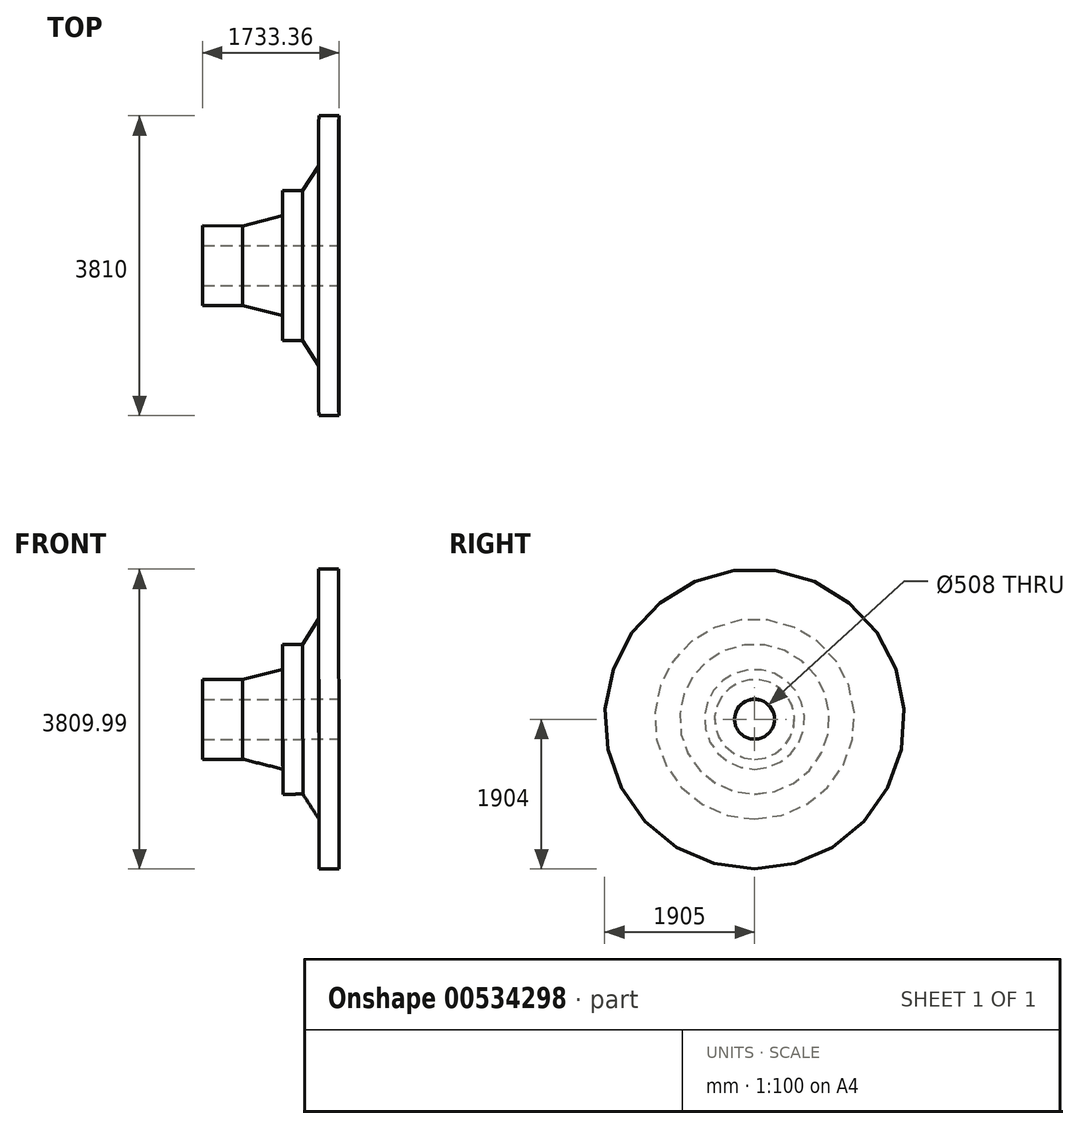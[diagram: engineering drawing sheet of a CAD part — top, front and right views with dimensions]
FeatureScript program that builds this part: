
annotation { "Feature Type Name" : "Feature", "Feature Type Description" : "" }
export const myFeature = defineFeature(function(context is Context, id is Id, definition is map)
    precondition{}
    {
        {
            var Q0;
            Q0=qCreatedBy(makeId("Front.planeOp"),FACE);
            var sketch = newSketch(context, id + "F0", { "sketchPlane" : qUnion([Q0])});
            skLineSegment(sketch, "E0", {"start": v(-1122.68, -2.8) * mm, "end": v(-1122.68, 251.2) * mm});
            skLineSegment(sketch, "E1", {"start": v(-1122.68, 251.2) * mm, "end": v(-614.68, 251.2) * mm});
            skLineSegment(sketch, "E2", {"start": v(-614.68, 251.2) * mm, "end": v(-106.68, 379.85) * mm});
            skLineSegment(sketch, "E3", {"start": v(-106.68, 379.85) * mm, "end": v(-106.68, 697.35) * mm});
            skLineSegment(sketch, "E4", {"start": v(-106.68, 697.35) * mm, "end": v(147.32, 697.35) * mm});
            skLineSegment(sketch, "E5", {"start": v(147.32, 697.35) * mm, "end": v(350.52, 1015.6) * mm});
            skLineSegment(sketch, "E6", {"start": v(350.52, 1015.6) * mm, "end": v(350.52, 1650.6) * mm});
            skLineSegment(sketch, "E7", {"start": v(350.52, 1650.6) * mm, "end": v(604.52, 1650.6) * mm});
            skLineSegment(sketch, "E8", {"start": v(604.52, 1650.6) * mm, "end": v(604.52, 0) * mm});
            skLineSegment(sketch, "E9", {"start": v(604.52, 0) * mm, "end": v(-1122.68, -2.8) * mm});
            skLineSegment(sketch, "E10", {"start": v(604.52, -254) * mm, "end": v(-1122.68, -256.8) * mm});
            skSolve(sketch);
        }
        {
            var Q0;
            Q0=makeQuery(id+"F0.imprint","IMPRINT",FACE,{"disambiguationData":[TD([[makeQuery(id+"F0.imprint","IMPRINT",EDGE,{"derivedFrom":sQuery(id+"F0.wireOp",EDGE,"E0")}),-1.0]])]});
            var Q1;
            Q1=sQuery(id+"F0.wireOp",EDGE,"E10");
            revolve(context, id + "F1", {"entities" : qUnion([Q0]), "axis" : qUnion([Q1]), "revolveType" : RevolveType.FULL});
        }
    });
